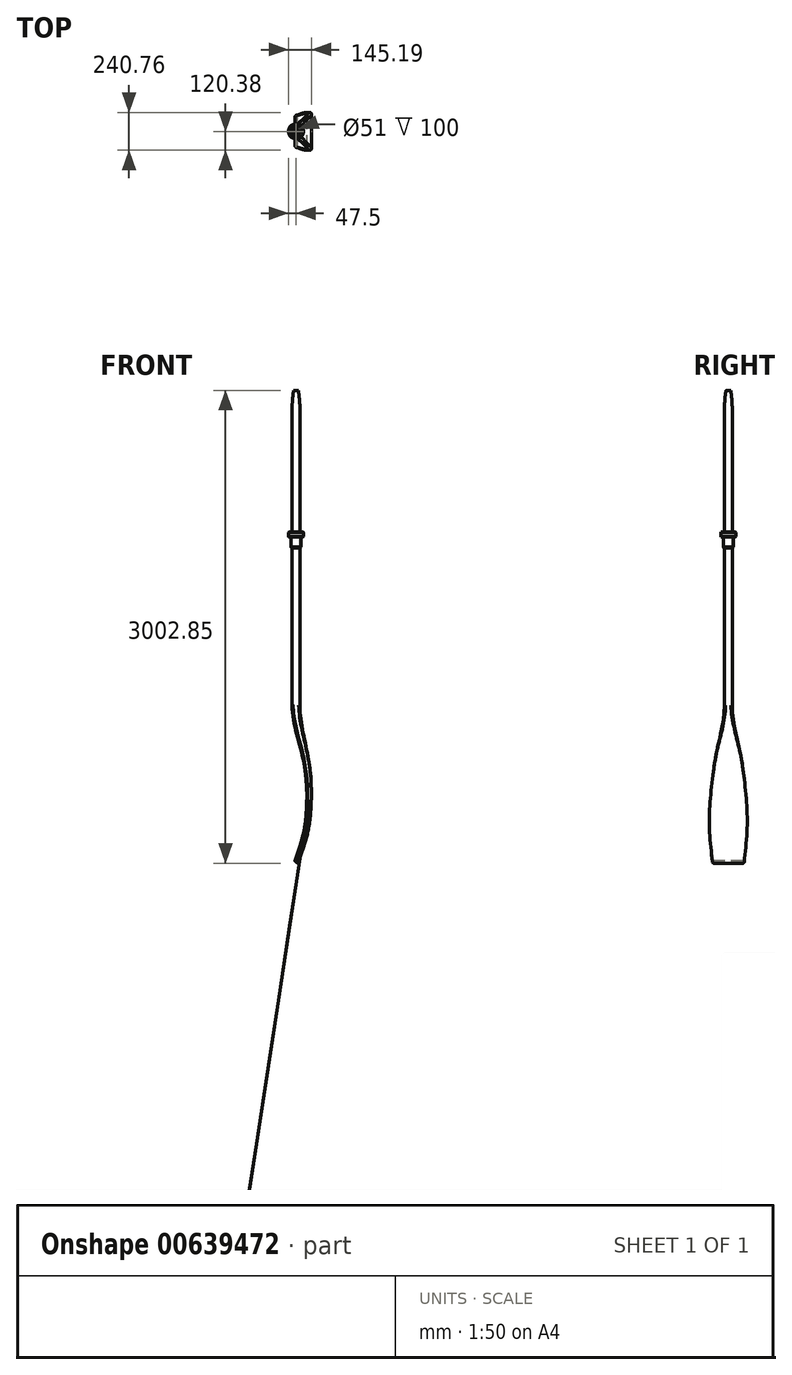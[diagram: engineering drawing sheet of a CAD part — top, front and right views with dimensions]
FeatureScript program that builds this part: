
annotation { "Feature Type Name" : "Feature", "Feature Type Description" : "" }
export const myFeature = defineFeature(function(context is Context, id is Id, definition is map)
    precondition{}
    {
        {
            var Q0;
            Q0=qCreatedBy(makeId("Front.planeOp"),FACE);
            var sketch = newSketch(context, id + "F0", { "sketchPlane" : qUnion([Q0])});
            skLineSegment(sketch, "E0", {"start": v(0, 0) * mm, "end": v(0, 2000) * mm, "construction": true});
            skLineSegment(sketch, "E1", {"start": v(-10.63, -997.15) * mm, "end": v(10.63, -1002.85) * mm, "construction": true});
            skLineSegment(sketch, "E2", {"start": v(0, 0) * mm, "end": v(0, -1000) * mm, "construction": true});
            skLineSegment(sketch, "E3", {"start": v(0, 2000) * mm, "end": v(15, 2000) * mm});
            skArc(sketch, "E4", {"start": v(25, 1870) * mm, "mid": v(22.5, 1935.2) * mm, "end": v(15, 2000) * mm});
            skLineSegment(sketch, "E5", {"start": v(0, 0) * mm, "end": v(25, 0) * mm});
            skLineSegment(sketch, "E6", {"start": v(25, 0) * mm, "end": v(25, 1870) * mm});
            skLineSegment(sketch, "E7", {"start": v(0, 2000) * mm, "end": v(0, 0) * mm});
            skLineSegment(sketch, "E8", {"start": v(25.5, 1000) * mm, "end": v(25.5, 1100) * mm});
            skLineSegment(sketch, "E9", {"start": v(25.5, 1100) * mm, "end": v(47.5, 1100) * mm});
            skLineSegment(sketch, "E10", {"start": v(47.5, 1100) * mm, "end": v(47.5, 1070) * mm});
            skLineSegment(sketch, "E11", {"start": v(47.5, 1070) * mm, "end": v(31.5, 1070) * mm});
            skLineSegment(sketch, "E12", {"start": v(31.5, 1070) * mm, "end": v(31.5, 1000) * mm});
            skLineSegment(sketch, "E13", {"start": v(31.5, 1000) * mm, "end": v(25.5, 1000) * mm});
            skFitSpline(sketch, "E14", {"points": [v(25, 0) * mm, v(94.15, -462.15) * mm, v(10.63, -1002.85) * mm], "startDerivative": vector(0, -845.45) * mm, "endDerivative": vector(-370.85, -526.93) * mm});
            skPoint(sketch, "E15", {"position": v(82.89, -767.35) * mm});
            skSolve(sketch);
        }
        {
            var Q0;
            Q0=makeQuery(id+"F0.imprint","IMPRINT",FACE,{"disambiguationData":[TD([[makeQuery(id+"F0.imprint","IMPRINT",EDGE,{"derivedFrom":sQuery(id+"F0.wireOp",EDGE,"E8")}),-1.0]])]});
            var Q1;
            Q1=sQuery(id+"F0.wireOp",EDGE,"E7");
            revolve(context, id + "F1", {"surfaceOperationType" : NewSurfaceOperationType.NEW, "entities" : qUnion([Q0]), "axis" : qUnion([Q1]), "revolveType" : RevolveType.FULL});
        }
        {
            var Q0;
            Q0=makeQuery(id+"F0.imprint","IMPRINT",FACE,{"disambiguationData":[TD([[makeQuery(id+"F0.imprint","IMPRINT",EDGE,{"derivedFrom":sQuery(id+"F0.wireOp",EDGE,"E3")}),-1.0]])]});
            var Q1;
            Q1=sQuery(id+"F0.wireOp",EDGE,"E7");
            revolve(context, id + "F2", {"surfaceOperationType" : NewSurfaceOperationType.NEW, "entities" : qUnion([Q0]), "axis" : qUnion([Q1]), "revolveType" : RevolveType.FULL});
        }
        {
            var Q0;
            Q0=makeQuery(id+"F1.opRevolve","SWEPT_EDGE",EDGE,{"disambiguationData":[OSD([sQuery(id+"F0.wireOp",EDGE,"E12"),sQuery(id+"F0.wireOp",EDGE,"E13")])]});
            chamfer(context, id + "F3", {"entities" : qUnion([Q0]), "width" : 5 * mm, "tangentPropagation" : true});
        }
        {
            var Q0;
            Q0=makeQuery(id+"F1.opRevolve","SWEPT_EDGE",EDGE,{"disambiguationData":[OSD([sQuery(id+"F0.wireOp",EDGE,"E9"),sQuery(id+"F0.wireOp",EDGE,"E10")])]});
            var Q1;
            Q1=makeQuery(id+"F1.opRevolve","SWEPT_EDGE",EDGE,{"disambiguationData":[OSD([sQuery(id+"F0.wireOp",EDGE,"E10"),sQuery(id+"F0.wireOp",EDGE,"E11")])]});
            chamfer(context, id + "F4", {"entities" : qUnion([Q0, Q1]), "width" : 2 * mm, "tangentPropagation" : true});
        }
        {
            var Q0;
            Q0=sQuery(id+"F0.wireOp",EDGE,"E14");
            var Q1;
            Q1=sQuery(id+"F0.wireOp",VERTEX,"E1.end");
            cPlane(context, id + "F5", {"entities" : qUnion([Q0, Q1]), "cplaneType" : CPlaneType.CURVE_POINT, "offset" : 25 * mm, "width" : 150 * mm, "height" : 150 * mm});
        }
        {
            var Q0;
            Q0=sQuery(id+"F0.wireOp",EDGE,"E14");
            var Q1;
            Q1=sQuery(id+"F0.wireOp",VERTEX,"E15");
            cPlane(context, id + "F6", {"entities" : qUnion([Q0, Q1]), "cplaneType" : CPlaneType.CURVE_POINT, "offset" : 25 * mm, "width" : 150 * mm, "height" : 150 * mm});
        }
        {
            var Q0;
            Q0=sQuery(id+"F0.wireOp",EDGE,"E14");
            var Q1;
            Q1=sQuery(id+"F0.wireOp",VERTEX,"E14.1.internal");
            cPlane(context, id + "F7", {"entities" : qUnion([Q0, Q1]), "cplaneType" : CPlaneType.CURVE_POINT, "offset" : 25 * mm, "width" : 150 * mm, "height" : 150 * mm});
        }
        {
            var Q0;
            Q0=qCreatedBy(id+"F5.planeOp",FACE);
            var sketch = newSketch(context, id + "F8", { "sketchPlane" : qUnion([Q0])});
            skLineSegment(sketch, "E16.bottom", {"start": v(565.21, 100) * mm, "end": v(585.87, 100) * mm});
            skLineSegment(sketch, "E16.top", {"start": v(565.21, -100) * mm, "end": v(585.87, -100) * mm});
            skLineSegment(sketch, "E16.left", {"start": v(565.21, 100) * mm, "end": v(565.21, -100) * mm});
            skLineSegment(sketch, "E16.right", {"start": v(585.87, 100) * mm, "end": v(585.87, -100) * mm});
            skSolve(sketch);
        }
        {
            var Q0;
            Q0=qCreatedBy(id+"F6.planeOp",FACE);
            var sketch = newSketch(context, id + "F9", { "sketchPlane" : qUnion([Q0])});
            skLineSegment(sketch, "E17.bottom", {"start": v(165.5, -120) * mm, "end": v(191.5, -120) * mm});
            skLineSegment(sketch, "E17.top", {"start": v(165.5, 120) * mm, "end": v(191.5, 120) * mm});
            skLineSegment(sketch, "E17.left", {"start": v(165.5, -120) * mm, "end": v(165.5, 120) * mm});
            skLineSegment(sketch, "E17.right", {"start": v(191.5, -120) * mm, "end": v(191.5, 120) * mm});
            skSolve(sketch);
        }
        {
            var Q0;
            Q0=qCreatedBy(id+"F7.planeOp",FACE);
            var sketch = newSketch(context, id + "F10", { "sketchPlane" : qUnion([Q0])});
            skLineSegment(sketch, "E18.bottom", {"start": v(29.72, -100) * mm, "end": v(59.72, -100) * mm});
            skLineSegment(sketch, "E18.top", {"start": v(29.72, 100) * mm, "end": v(59.72, 100) * mm});
            skLineSegment(sketch, "E18.left", {"start": v(29.72, -100) * mm, "end": v(29.72, 100) * mm});
            skLineSegment(sketch, "E18.right", {"start": v(59.72, -100) * mm, "end": v(59.72, 100) * mm});
            skSolve(sketch);
        }
        {
            var Q0;
            Q0=makeQuery(id+"F2.opRevolve","SWEPT_FACE",FACE,{"disambiguationData":[OSD([sQuery(id+"F0.wireOp",EDGE,"E5")])]});
            var sketch = newSketch(context, id + "F11", { "sketchPlane" : qUnion([Q0])});
            skLineSegment(sketch, "E19", {"start": v(-17.68, -17.68) * mm, "end": v(17.68, 17.68) * mm, "construction": true});
            skLineSegment(sketch, "E20", {"start": v(17.68, -17.68) * mm, "end": v(-17.68, 17.68) * mm, "construction": true});
            skSolve(sketch);
        }
        {
            var Q0;
            Q0=sQuery(id+"F0.wireOp",EDGE,"E14");
            var Q2;
            Q2=makeQuery(id+"F11.imprint","IMPRINT",FACE,{"disambiguationData":[TD([[makeQuery(id+"F11.imprint","IMPRINT",EDGE,{"derivedFrom":makeQuery(id+"F2.opRevolve","SWEPT_EDGE",EDGE,{"disambiguationData":[OSD([sQuery(id+"F0.wireOp",EDGE,"E5"),sQuery(id+"F0.wireOp",EDGE,"E6")])]})}),-1.0]])]});
            var Q3;
            Q3=makeQuery(id+"F10.imprint","IMPRINT",FACE,{"disambiguationData":[TD([[makeQuery(id+"F10.imprint","IMPRINT",EDGE,{"derivedFrom":sQuery(id+"F10.wireOp",EDGE,"E18.bottom")}),1.0]])]});
            var Q4;
            Q4=makeQuery(id+"F9.imprint","IMPRINT",FACE,{"disambiguationData":[TD([[makeQuery(id+"F9.imprint","IMPRINT",EDGE,{"derivedFrom":sQuery(id+"F9.wireOp",EDGE,"E17.bottom")}),1.0]])]});
            var Q5;
            Q5=makeQuery(id+"F8.imprint","IMPRINT",FACE,{"disambiguationData":[TD([[makeQuery(id+"F8.imprint","IMPRINT",EDGE,{"derivedFrom":sQuery(id+"F8.wireOp",EDGE,"E16.bottom")}),-1.0]])]});
            var Q6;
            Q6=sQuery(id+"F11.wireOp",VERTEX,"E20.end");
            var Q7;
            Q7=sQuery(id+"F10.wireOp",VERTEX,"E18.top.start");
            var Q8;
            Q8=sQuery(id+"F9.wireOp",VERTEX,"E17.top.start");
            var Q9;
            Q9=sQuery(id+"F8.wireOp",VERTEX,"E16.bottom.start");
            loft(context, id + "F12", {"operationType" : NewBodyOperationType.ADD, "addSections" : true, "spine" : qUnion([Q0]), "sectionCount" : 2, "startCondition" : LoftEndDerivativeType.NORMAL_TO_PROFILE, "startMagnitude" : 1, "sheetProfilesArray" : [{ "sheetProfileEntities" : qUnion([Q2]) }, { "sheetProfileEntities" : qUnion([Q3]) }, { "sheetProfileEntities" : qUnion([Q4]) }, { "sheetProfileEntities" : qUnion([Q5]) }], "matchConnections" : true, "connections" : [{ "connectionEntities" : qUnion([Q6, Q7, Q8, Q9]), "connectionEdgeQueries" : qUnion([]), "connectionEdgeParameters" : [] }]});
        }
        {
            var Q0;
            Q0=makeQuery(id+"F12.opLoft","MID_CAP_EDGE",EDGE,{"disambiguationData":[OSD([sQuery(id+"F8.wireOp",EDGE,"E16.bottom"),sQuery(id+"F8.wireOp",EDGE,"E16.left"),sQuery(id+"F8.wireOp",EDGE,"E16.right")])],"capPos":3.0});
            var Q1;
            Q1=makeQuery(id+"F12.opLoft","MID_CAP_EDGE",EDGE,{"disambiguationData":[OSD([sQuery(id+"F8.wireOp",EDGE,"E16.top"),sQuery(id+"F8.wireOp",EDGE,"E16.left"),sQuery(id+"F8.wireOp",EDGE,"E16.right")])],"capPos":3.0});
            fillet(context, id + "F13", {"entities" : qUnion([Q0, Q1]), "radius" : 8 * mm, "tangentPropagation" : true, "allowEdgeOverflow" : false});
        }
        {
            var Q0;
            Q0=makeQuery(id+"F12.opLoft","SWEPT_EDGE",EDGE,{"disambiguationData":[OSD([sQuery(id+"F8.wireOp",EDGE,"E16.bottom"),sQuery(id+"F8.wireOp",EDGE,"E16.left"),sQuery(id+"F9.wireOp",EDGE,"E17.top"),sQuery(id+"F9.wireOp",EDGE,"E17.left"),sQuery(id+"F10.wireOp",EDGE,"E18.top"),sQuery(id+"F10.wireOp",EDGE,"E18.left"),sQuery(id+"F11.wireOp",VERTEX,"E20.end")])]});
            fillet(context, id + "F14", {"entities" : qUnion([Q0]), "radius" : 5 * mm, "tangentPropagation" : true, "rho" : 0.5, "crossSection" : FilletCrossSection.CONIC, "allowEdgeOverflow" : false});
        }
    });
